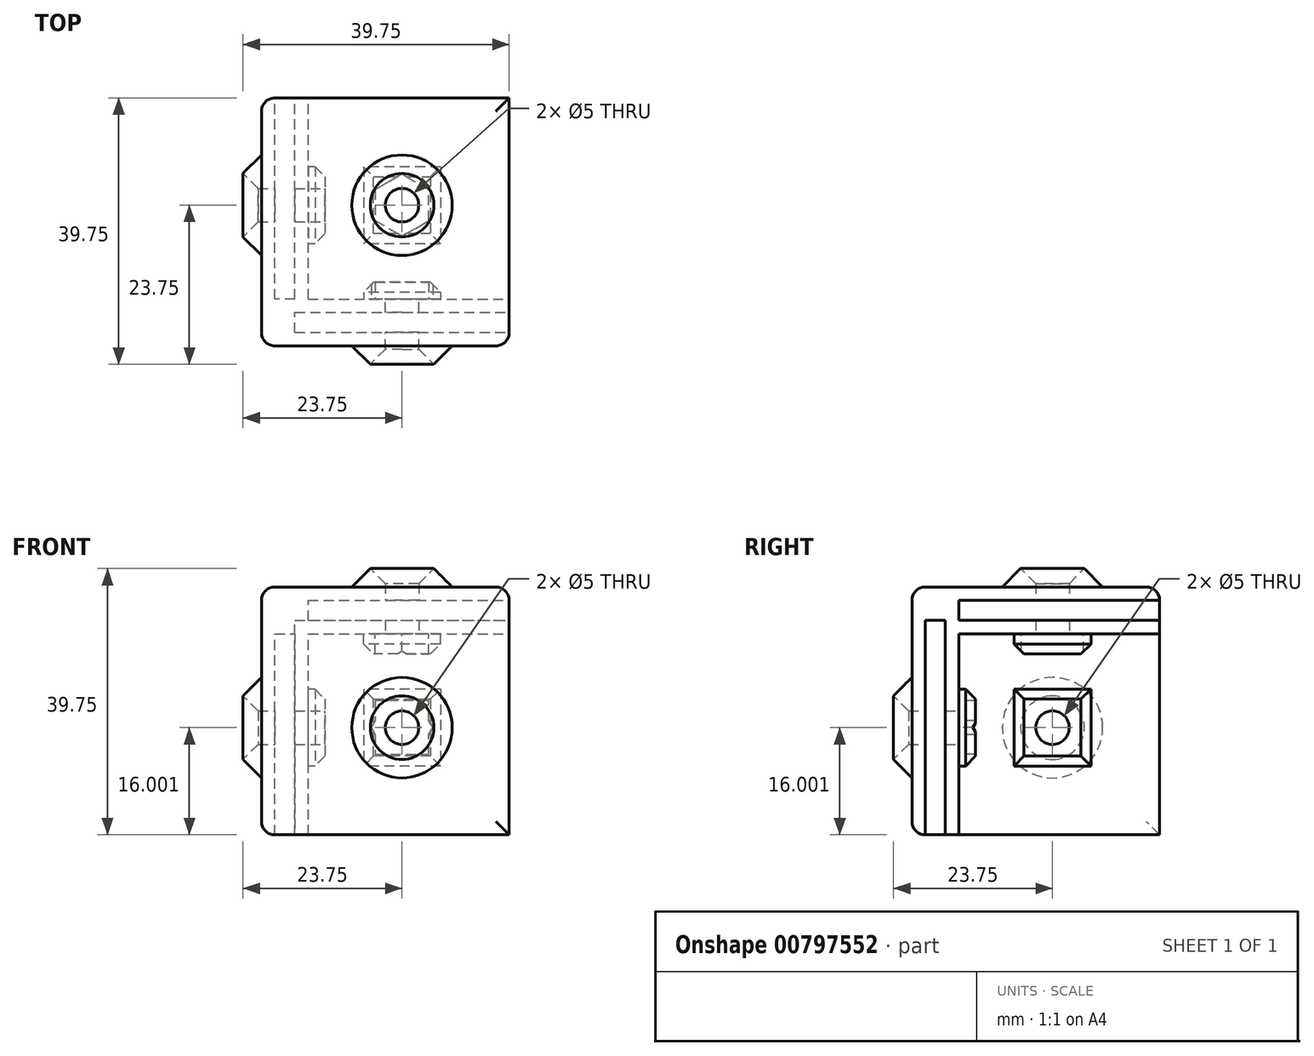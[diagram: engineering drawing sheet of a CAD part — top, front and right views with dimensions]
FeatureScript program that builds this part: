
annotation { "Feature Type Name" : "Feature", "Feature Type Description" : "" }
export const myFeature = defineFeature(function(context is Context, id is Id, definition is map)
    precondition{}
    {
        {
            var Q0;
            Q0=qCreatedBy(makeId("Right.planeOp"),FACE);
            var sketch = newSketch(context, id + "F0", { "sketchPlane" : qUnion([Q0])});
            skLineSegment(sketch, "E0.bottom", {"start": v(0, 0.7) * mm, "end": v(37, 0.7) * mm});
            skLineSegment(sketch, "E0.top", {"start": v(0, 37.7) * mm, "end": v(37, 37.7) * mm});
            skLineSegment(sketch, "E0.left", {"start": v(0, 0.7) * mm, "end": v(0, 37.7) * mm});
            skLineSegment(sketch, "E0.right", {"start": v(37, 0.7) * mm, "end": v(37, 37.7) * mm});
            skSolve(sketch);
        }
        {
            var Q0;
            Q0 = qSketchRegion(id + "F0", true);
            extrude(context, id + "F1", {"entities" : qUnion([Q0]), "depth" : 37 * mm, "offsetDistance" : 25 * mm});
        }
        {
            var Q0;
            Q0=makeQuery(id+"F1.opExtrude","CAP_FACE",FACE,{"disambiguationData":[OSD([sQuery(id+"F0.wireOp",EDGE,"E0.bottom"),sQuery(id+"F0.wireOp",EDGE,"E0.top"),sQuery(id+"F0.wireOp",EDGE,"E0.left"),sQuery(id+"F0.wireOp",EDGE,"E0.right")])],"isStart":false});
            var sketch = newSketch(context, id + "F2", { "sketchPlane" : qUnion([Q0])});
            skLineSegment(sketch, "E1", {"start": v(0, 0.7) * mm, "end": v(2, 0.7) * mm});
            skLineSegment(sketch, "E2", {"start": v(2, 0.7) * mm, "end": v(2, 30.7) * mm});
            skLineSegment(sketch, "E3", {"start": v(2, 30.7) * mm, "end": v(5, 30.7) * mm});
            skLineSegment(sketch, "E4", {"start": v(5, 30.7) * mm, "end": v(5, 0.7) * mm});
            skLineSegment(sketch, "E5", {"start": v(37, 37.7) * mm, "end": v(37, 35.7) * mm});
            skLineSegment(sketch, "E6", {"start": v(37, 35.7) * mm, "end": v(7, 35.7) * mm});
            skLineSegment(sketch, "E7", {"start": v(7, 35.7) * mm, "end": v(7, 32.7) * mm});
            skLineSegment(sketch, "E8", {"start": v(7, 32.7) * mm, "end": v(37, 32.7) * mm});
            skLineSegment(sketch, "E9", {"start": v(5, 0.7) * mm, "end": v(7, 0.7) * mm});
            skLineSegment(sketch, "E10", {"start": v(7, 0.7) * mm, "end": v(7, 30.7) * mm});
            skLineSegment(sketch, "E11", {"start": v(7, 30.7) * mm, "end": v(37, 30.7) * mm});
            skSolve(sketch);
        }
        {
            var Q0;
            Q0 = qSketchRegion(id + "F2", true);
            var Q1;
            {var subQ0=sQuery(id+"F2.wireOp",EDGE,"E10");Q1=makeQuery(id+"F2.imprint","IMPRINT",FACE,{"disambiguationData":[TD([[makeQuery(id+"F2.imprint","IMPRINT",EDGE,{"derivedFrom":subQ0}),-1.0]])]});}
            var Q2;
            {var subQ0=sQuery(id+"F2.wireOp",EDGE,"E2");Q2=makeQuery(id+"F2.imprint","IMPRINT",FACE,{"disambiguationData":[TD([[makeQuery(id+"F2.imprint","IMPRINT",EDGE,{"derivedFrom":subQ0}),-1.0]])]});}
            var Q3;
            {var subQ0=sQuery(id+"F2.wireOp",EDGE,"E6");Q3=makeQuery(id+"F2.imprint","IMPRINT",FACE,{"disambiguationData":[TD([[makeQuery(id+"F2.imprint","IMPRINT",EDGE,{"derivedFrom":subQ0}),1.0]])]});}
            extrude(context, id + "F3", {"entities" : qUnion([Q0, Q1, Q2, Q3]), "operationType" : NewBodyOperationType.REMOVE, "oppositeDirection" : true, "depth" : 30 * mm, "offsetDistance" : 25 * mm});
        }
        {
            var Q0;
            Q0=makeQuery(id+"F1.opExtrude","SWEPT_FACE",FACE,{"disambiguationData":[OSD([sQuery(id+"F0.wireOp",EDGE,"E0.right")])]});
            var sketch = newSketch(context, id + "F4", { "sketchPlane" : qUnion([Q0])});
            skLineSegment(sketch, "E12", {"start": v(0, 0.7) * mm, "end": v(-2, 0.7) * mm});
            skLineSegment(sketch, "E13", {"start": v(-2, 0.7) * mm, "end": v(-2, 30.7) * mm});
            skLineSegment(sketch, "E14", {"start": v(-2, 30.7) * mm, "end": v(-5, 30.7) * mm});
            skLineSegment(sketch, "E15", {"start": v(-5, 30.7) * mm, "end": v(-5, 0.7) * mm});
            skSolve(sketch);
        }
        {
            var Q0;
            Q0 = qSketchRegion(id + "F4", true);
            var Q1;
            {var subQ0=sQuery(id+"F4.wireOp",EDGE,"E13");Q1=makeQuery(id+"F4.imprint","IMPRINT",FACE,{"disambiguationData":[TD([[makeQuery(id+"F4.imprint","IMPRINT",EDGE,{"derivedFrom":subQ0}),1.0]])]});}
            extrude(context, id + "F5", {"entities" : qUnion([Q0, Q1]), "operationType" : NewBodyOperationType.REMOVE, "oppositeDirection" : true, "depth" : 30 * mm, "offsetDistance" : 25 * mm});
        }
        {
            var Q0;
            Q0=makeQuery(id+"F1.opExtrude","CAP_EDGE",EDGE,{"disambiguationData":[OSD([sQuery(id+"F0.wireOp",EDGE,"E0.top")])],"isStart":true});
            var Q1;
            Q1=makeQuery(id+"F1.opExtrude","SWEPT_FACE",FACE,{"disambiguationData":[OSD([sQuery(id+"F0.wireOp",EDGE,"E0.left")])]});
            var Q2;
            Q2=makeQuery(id+"F1.opExtrude","CAP_EDGE",EDGE,{"disambiguationData":[OSD([sQuery(id+"F0.wireOp",EDGE,"E0.top")])],"isStart":false});
            var Q3;
            Q3=makeQuery(id+"F1.opExtrude","SWEPT_EDGE",EDGE,{"disambiguationData":[OSD([sQuery(id+"F0.wireOp",EDGE,"E0.top"),sQuery(id+"F0.wireOp",EDGE,"E0.right")])]});
            var Q4;
            Q4=makeQuery(id+"F1.opExtrude","CAP_EDGE",EDGE,{"disambiguationData":[OSD([sQuery(id+"F0.wireOp",EDGE,"E0.right")])],"isStart":true});
            var Q5;
            Q5=makeQuery(id+"F1.opExtrude","CAP_EDGE",EDGE,{"disambiguationData":[OSD([sQuery(id+"F0.wireOp",EDGE,"E0.bottom")])],"isStart":true});
            var Q6;
            {var subQ0=sQuery(id+"F0.wireOp",EDGE,"E0.bottom");var subQ1=makeQuery(id+"F1.opExtrude","CAP_EDGE",EDGE,{"disambiguationData":[OSD([subQ0])],"isStart":false});Q6=makeQuery(id+"F3.boolean.opBoolean","COPY",EDGE,{"derivedFrom":makeQuery(id+"F3.opExtrude","CAP_EDGE",EDGE,{"disambiguationData":[OSD([subQ0]),TDD([makeQuery(id+"F2.imprint","IMPRINT",EDGE,{"disambiguationData":[TD([[makeQuery(id+"F2.imprint","INTERSECT",VERTEX,{"derivedFrom":[subQ1,makeQuery(id+"F1.opExtrude","CAP_EDGE",EDGE,{"disambiguationData":[OSD([sQuery(id+"F0.wireOp",EDGE,"E0.right")])],"isStart":false})]}),1.0]])],"derivedFrom":subQ1})])],"isStart":false})});}
            var Q7;
            {var subQ0=sQuery(id+"F0.wireOp",EDGE,"E0.right");var subQ1=makeQuery(id+"F1.opExtrude","CAP_EDGE",EDGE,{"disambiguationData":[OSD([subQ0])],"isStart":false});Q7=makeQuery(id+"F3.boolean.opBoolean","COPY",EDGE,{"derivedFrom":makeQuery(id+"F3.opExtrude","CAP_EDGE",EDGE,{"disambiguationData":[OSD([subQ0]),TDD([makeQuery(id+"F2.imprint","IMPRINT",EDGE,{"disambiguationData":[TD([[makeQuery(id+"F2.imprint","INTERSECT",VERTEX,{"derivedFrom":[makeQuery(id+"F1.opExtrude","CAP_EDGE",EDGE,{"disambiguationData":[OSD([sQuery(id+"F0.wireOp",EDGE,"E0.bottom")])],"isStart":false}),subQ1]}),-1.0]])],"derivedFrom":subQ1})])],"isStart":false})});}
            var Q8;
            Q8=makeQuery(id+"F3.boolean.opBoolean","COPY",EDGE,{"derivedFrom":makeQuery(id+"F3.opExtrude","SWEPT_EDGE",EDGE,{"disambiguationData":[OSD([sQuery(id+"F0.wireOp",EDGE,"E0.right"),sQuery(id+"F2.wireOp",EDGE,"E11")])]})});
            var Q9;
            Q9=makeQuery(id+"F3.boolean.opBoolean","COPY",EDGE,{"derivedFrom":makeQuery(id+"F3.opExtrude","CAP_EDGE",EDGE,{"disambiguationData":[OSD([sQuery(id+"F2.wireOp",EDGE,"E11")])],"isStart":true})});
            var Q10;
            Q10=makeQuery(id+"F3.boolean.opBoolean","COPY",EDGE,{"derivedFrom":makeQuery(id+"F3.opExtrude","SWEPT_EDGE",EDGE,{"disambiguationData":[OSD([sQuery(id+"F0.wireOp",EDGE,"E0.bottom"),sQuery(id+"F2.wireOp",EDGE,"E9"),sQuery(id+"F2.wireOp",EDGE,"E10")])]})});
            var Q11;
            Q11=makeQuery(id+"F3.boolean.opBoolean","COPY",EDGE,{"derivedFrom":makeQuery(id+"F3.opExtrude","CAP_EDGE",EDGE,{"disambiguationData":[OSD([sQuery(id+"F2.wireOp",EDGE,"E10")])],"isStart":true})});
            fillet(context, id + "F6", {"entities" : qUnion([Q0, Q1, Q2, Q3, Q4, Q5, Q6, Q7, Q8, Q9, Q10, Q11]), "radius" : 2 * mm, "tangentPropagation" : true, "allowEdgeOverflow" : false});
        }
        {
            var Q0;
            Q0=makeQuery(id+"F3.boolean.opBoolean","COPY",FACE,{"derivedFrom":makeQuery(id+"F3.opExtrude","SWEPT_FACE",FACE,{"disambiguationData":[OSD([sQuery(id+"F2.wireOp",EDGE,"E10")])]})});
            var sketch = newSketch(context, id + "F7", { "sketchPlane" : qUnion([Q0])});
            skCircle(sketch, "E16", {"center": v(-21, 16.7) * mm, "radius": 2.5 * mm});
            skSolve(sketch);
        }
        {
            var Q0;
            Q0=makeQuery(id+"F7.imprint","IMPRINT",FACE,{"disambiguationData":[TD([[makeQuery(id+"F7.imprint","IMPRINT",EDGE,{"derivedFrom":sQuery(id+"F7.wireOp",EDGE,"E16")}),1.0]])]});
            extrude(context, id + "F8", {"entities" : qUnion([Q0]), "operationType" : NewBodyOperationType.REMOVE, "oppositeDirection" : true, "depth" : 25 * mm, "offsetDistance" : 25 * mm});
        }
        {
            var Q0;
            Q0=makeQuery(id+"F1.opExtrude","SWEPT_FACE",FACE,{"disambiguationData":[OSD([sQuery(id+"F0.wireOp",EDGE,"E0.left")])]});
            var sketch = newSketch(context, id + "F9", { "sketchPlane" : qUnion([Q0])});
            skCircle(sketch, "E17", {"center": v(21, 16.7) * mm, "radius": 7.5 * mm});
            skSolve(sketch);
        }
        {
            var Q0;
            Q0=makeQuery(id+"F9.imprint","IMPRINT",FACE,{"disambiguationData":[TD([[makeQuery(id+"F9.imprint","IMPRINT",EDGE,{"derivedFrom":sQuery(id+"F9.wireOp",EDGE,"E17")}),1.0]])]});
            extrude(context, id + "F10", {"entities" : qUnion([Q0]), "operationType" : NewBodyOperationType.ADD, "depth" : 3 * mm, "offsetDistance" : 25 * mm});
        }
        {
            var Q0;
            Q0=makeQuery(id+"F10.opExtrude","CAP_EDGE",EDGE,{"disambiguationData":[OSD([sQuery(id+"F0.wireOp",EDGE,"E0.left"),sQuery(id+"F7.wireOp",EDGE,"E16")])],"isStart":false});
            chamfer(context, id + "F11", {"entities" : qUnion([Q0]), "width" : 2.5 * mm, "tangentPropagation" : true});
        }
        {
            var Q0;
            Q0=makeQuery(id+"F3.boolean.opBoolean","COPY",FACE,{"derivedFrom":makeQuery(id+"F3.opExtrude","SWEPT_FACE",FACE,{"disambiguationData":[OSD([sQuery(id+"F2.wireOp",EDGE,"E10")])]})});
            var sketch = newSketch(context, id + "F12", { "sketchPlane" : qUnion([Q0])});
            skLineSegment(sketch, "E18", {"start": v(-25, 16.7) * mm, "end": v(-25, 20.7) * mm});
            skLineSegment(sketch, "E19", {"start": v(-25, 20.7) * mm, "end": v(-17, 20.7) * mm});
            skLineSegment(sketch, "E20", {"start": v(-17, 20.7) * mm, "end": v(-17, 12.7) * mm});
            skLineSegment(sketch, "E21", {"start": v(-17, 12.7) * mm, "end": v(-25, 12.7) * mm});
            skLineSegment(sketch, "E22", {"start": v(-25, 12.7) * mm, "end": v(-25, 16.7) * mm});
            skLineSegment(sketch, "E23.bottom", {"start": v(-26.75, 22.45) * mm, "end": v(-15.25, 22.45) * mm});
            skLineSegment(sketch, "E23.top", {"start": v(-26.75, 10.95) * mm, "end": v(-15.25, 10.95) * mm});
            skLineSegment(sketch, "E23.left", {"start": v(-26.75, 22.45) * mm, "end": v(-26.75, 10.95) * mm});
            skLineSegment(sketch, "E23.right", {"start": v(-15.25, 22.45) * mm, "end": v(-15.25, 10.95) * mm});
            skPoint(sketch, "E23.middle", {"position": v(-21, 16.7) * mm});
            skLineSegment(sketch, "E24", {"start": v(-25, 20.7) * mm, "end": v(-22.66, 20.7) * mm});
            skLineSegment(sketch, "E25", {"start": v(-25, 20.7) * mm, "end": v(-25, 18.36) * mm});
            skLineSegment(sketch, "E26", {"start": v(-17, 12.7) * mm, "end": v(-19.34, 12.7) * mm});
            skLineSegment(sketch, "E27", {"start": v(-17, 12.7) * mm, "end": v(-17, 15.04) * mm});
            skLineSegment(sketch, "E28", {"start": v(-25, 12.7) * mm, "end": v(-25, 15.04) * mm});
            skLineSegment(sketch, "E29", {"start": v(-17, 20.7) * mm, "end": v(-19.34, 20.7) * mm});
            skLineSegment(sketch, "E30", {"start": v(-17, 18.36) * mm, "end": v(-17, 20.7) * mm});
            skLineSegment(sketch, "E31", {"start": v(-19.34, 12.7) * mm, "end": v(-22.66, 12.7) * mm});
            skCircle(sketch, "E32.cCircle", {"center": v(-21, 16.7) * mm, "radius": 4 * mm, "construction": true});
            skLineSegment(sketch, "E32.0", {"start": v(-23.3, 20.7) * mm, "end": v(-18.7, 20.7) * mm});
            skLineSegment(sketch, "E32.1", {"start": v(-18.7, 20.7) * mm, "end": v(-16.38, 16.7) * mm});
            skLineSegment(sketch, "E32.2", {"start": v(-16.38, 16.7) * mm, "end": v(-18.7, 12.7) * mm});
            skLineSegment(sketch, "E32.3", {"start": v(-18.7, 12.7) * mm, "end": v(-23.3, 12.7) * mm});
            skLineSegment(sketch, "E32.4", {"start": v(-23.3, 12.7) * mm, "end": v(-25.62, 16.7) * mm});
            skLineSegment(sketch, "E32.5", {"start": v(-25.62, 16.7) * mm, "end": v(-23.3, 20.7) * mm});
            skPoint(sketch, "E32.0.midPoint", {"position": v(-21, 20.7) * mm});
            skSolve(sketch);
        }
        {
            var Q0;
            {var subQ0=sQuery(id+"F12.wireOp",EDGE,"E28");Q0=makeQuery(id+"F12.imprint","IMPRINT",FACE,{"disambiguationData":[TD([[makeQuery(id+"F12.imprint","IMPRINT",EDGE,{"derivedFrom":subQ0}),-1.0]])]});}
            var Q1;
            Q1=makeQuery(id+"F12.imprint","IMPRINT",FACE,{"disambiguationData":[TD([[makeQuery(id+"F12.imprint","IMPRINT",EDGE,{"derivedFrom":sQuery(id+"F12.wireOp",EDGE,"E26")}),-1.0]])]});
            var Q2;
            {var subQ18=sQuery(id+"F12.wireOp",EDGE,"E21");Q2=makeQuery(id+"F12.imprint","IMPRINT",FACE,{"disambiguationData":[TD([[makeQuery(id+"F12.imprint","IMPRINT",EDGE,{"derivedFrom":subQ18}),1.0]])]});}
            var Q3;
            {var subQ4=sQuery(id+"F12.wireOp",EDGE,"E24");Q3=makeQuery(id+"F12.imprint","IMPRINT",FACE,{"disambiguationData":[TD([[makeQuery(id+"F12.imprint","IMPRINT",EDGE,{"derivedFrom":subQ4}),-1.0]])]});}
            var Q4;
            {var subQ4=sQuery(id+"F12.wireOp",EDGE,"E29");Q4=makeQuery(id+"F12.imprint","IMPRINT",FACE,{"disambiguationData":[TD([[makeQuery(id+"F12.imprint","IMPRINT",EDGE,{"derivedFrom":subQ4}),1.0]])]});}
            extrude(context, id + "F13", {"entities" : qUnion([Q0, Q1, Q2, Q3, Q4]), "operationType" : NewBodyOperationType.ADD, "depth" : 2.5 * mm, "offsetDistance" : 25 * mm});
        }
        {
            var Q0;
            Q0=makeQuery(id+"F13.opExtrude","CAP_EDGE",EDGE,{"disambiguationData":[OSD([sQuery(id+"F12.wireOp",EDGE,"E23.left")])],"isStart":false});
            var Q1;
            Q1=makeQuery(id+"F13.opExtrude","CAP_EDGE",EDGE,{"disambiguationData":[OSD([sQuery(id+"F12.wireOp",EDGE,"E23.top")])],"isStart":false});
            var Q2;
            Q2=makeQuery(id+"F13.opExtrude","CAP_EDGE",EDGE,{"disambiguationData":[OSD([sQuery(id+"F12.wireOp",EDGE,"E23.right")])],"isStart":false});
            var Q3;
            Q3=makeQuery(id+"F13.opExtrude","CAP_EDGE",EDGE,{"disambiguationData":[OSD([sQuery(id+"F12.wireOp",EDGE,"E23.bottom")])],"isStart":false});
            chamfer(context, id + "F14", {"entities" : qUnion([Q0, Q1, Q2, Q3]), "width" : 1.5 * mm, "tangentPropagation" : true});
        }
        {
            var Q0;
            Q0=makeQuery(id+"F3.boolean.opBoolean","COPY",FACE,{"derivedFrom":makeQuery(id+"F3.opExtrude","CAP_FACE",FACE,{"disambiguationData":[OSD([sQuery(id+"F0.wireOp",EDGE,"E0.bottom"),sQuery(id+"F0.wireOp",EDGE,"E0.right"),sQuery(id+"F2.wireOp",EDGE,"E10"),sQuery(id+"F2.wireOp",EDGE,"E11")])],"isStart":false})});
            var sketch = newSketch(context, id + "F15", { "sketchPlane" : qUnion([Q0])});
            skLineSegment(sketch, "E33", {"start": v(21, 2.7) * mm, "end": v(21, 16.7) * mm});
            skCircle(sketch, "E34", {"center": v(21, 16.7) * mm, "radius": 2.5 * mm});
            skSolve(sketch);
        }
        {
            var Q0;
            Q0=makeQuery(id+"F15.imprint","IMPRINT",FACE,{"disambiguationData":[TD([[makeQuery(id+"F15.imprint","IMPRINT",EDGE,{"derivedFrom":sQuery(id+"F15.wireOp",EDGE,"E34")}),1.0]])]});
            extrude(context, id + "F16", {"entities" : qUnion([Q0]), "operationType" : NewBodyOperationType.REMOVE, "oppositeDirection" : true, "depth" : 25 * mm, "offsetDistance" : 25 * mm});
        }
        {
            var Q0;
            Q0=makeQuery(id+"F1.opExtrude","CAP_FACE",FACE,{"disambiguationData":[OSD([sQuery(id+"F0.wireOp",EDGE,"E0.bottom"),sQuery(id+"F0.wireOp",EDGE,"E0.top"),sQuery(id+"F0.wireOp",EDGE,"E0.left"),sQuery(id+"F0.wireOp",EDGE,"E0.right")])],"isStart":true});
            var sketch = newSketch(context, id + "F17", { "sketchPlane" : qUnion([Q0])});
            skCircle(sketch, "E35", {"center": v(-21, 16.7) * mm, "radius": 7.5 * mm});
            skSolve(sketch);
        }
        {
            var Q0;
            Q0=makeQuery(id+"F17.imprint","IMPRINT",FACE,{"disambiguationData":[TD([[makeQuery(id+"F17.imprint","IMPRINT",EDGE,{"derivedFrom":sQuery(id+"F17.wireOp",EDGE,"E35")}),1.0]])]});
            extrude(context, id + "F18", {"entities" : qUnion([Q0]), "operationType" : NewBodyOperationType.ADD, "depth" : 3 * mm, "offsetDistance" : 25 * mm});
        }
        {
            var Q0;
            Q0=makeQuery(id+"F18.opExtrude","CAP_EDGE",EDGE,{"disambiguationData":[OSD([sQuery(id+"F0.wireOp",EDGE,"E0.bottom"),sQuery(id+"F0.wireOp",EDGE,"E0.top"),sQuery(id+"F0.wireOp",EDGE,"E0.left"),sQuery(id+"F0.wireOp",EDGE,"E0.right"),sQuery(id+"F15.wireOp",EDGE,"E34")])],"isStart":false});
            chamfer(context, id + "F19", {"entities" : qUnion([Q0]), "width" : 2.5 * mm, "tangentPropagation" : true});
        }
        {
            var Q0;
            Q0=makeQuery(id+"F3.boolean.opBoolean","COPY",FACE,{"derivedFrom":makeQuery(id+"F3.opExtrude","CAP_FACE",FACE,{"disambiguationData":[OSD([sQuery(id+"F0.wireOp",EDGE,"E0.bottom"),sQuery(id+"F0.wireOp",EDGE,"E0.right"),sQuery(id+"F2.wireOp",EDGE,"E10"),sQuery(id+"F2.wireOp",EDGE,"E11")])],"isStart":false})});
            var sketch = newSketch(context, id + "F20", { "sketchPlane" : qUnion([Q0])});
            skLineSegment(sketch, "E36.bottom", {"start": v(26.75, 10.95) * mm, "end": v(15.25, 10.95) * mm});
            skLineSegment(sketch, "E36.top", {"start": v(26.75, 22.45) * mm, "end": v(15.25, 22.45) * mm});
            skLineSegment(sketch, "E36.left", {"start": v(26.75, 10.95) * mm, "end": v(26.75, 22.45) * mm});
            skLineSegment(sketch, "E36.right", {"start": v(15.25, 10.95) * mm, "end": v(15.25, 22.45) * mm});
            skPoint(sketch, "E36.middle", {"position": v(21, 16.7) * mm});
            skLineSegment(sketch, "E37.top", {"start": v(25, 20.7) * mm, "end": v(17, 20.7) * mm});
            skLineSegment(sketch, "E38", {"start": v(22.66, 12.7) * mm, "end": v(22.57, 12.62) * mm});
            skLineSegment(sketch, "E39", {"start": v(25, 20.7) * mm, "end": v(22.66, 20.7) * mm});
            skLineSegment(sketch, "E40", {"start": v(25, 20.7) * mm, "end": v(25, 18.36) * mm});
            skCircle(sketch, "E41.cCircle", {"center": v(21, 16.7) * mm, "radius": 4 * mm, "construction": true});
            skLineSegment(sketch, "E41.0", {"start": v(18.7, 20.7) * mm, "end": v(23.3, 20.7) * mm});
            skLineSegment(sketch, "E41.1", {"start": v(23.3, 20.7) * mm, "end": v(25.62, 16.7) * mm});
            skLineSegment(sketch, "E41.2", {"start": v(25.62, 16.7) * mm, "end": v(23.3, 12.7) * mm});
            skLineSegment(sketch, "E41.3", {"start": v(23.3, 12.7) * mm, "end": v(18.7, 12.7) * mm});
            skLineSegment(sketch, "E41.4", {"start": v(18.7, 12.7) * mm, "end": v(16.38, 16.7) * mm});
            skLineSegment(sketch, "E41.5", {"start": v(16.38, 16.7) * mm, "end": v(18.7, 20.7) * mm});
            skPoint(sketch, "E41.0.midPoint", {"position": v(21, 20.7) * mm});
            skSolve(sketch);
        }
        {
            var Q0;
            Q0=makeQuery(id+"F20.imprint","IMPRINT",FACE,{"disambiguationData":[TD([[makeQuery(id+"F20.imprint","IMPRINT",EDGE,{"derivedFrom":sQuery(id+"F20.wireOp",EDGE,"E36.bottom")}),-1.0]])]});
            var Q1;
            {var subQ0=sQuery(id+"F20.wireOp",EDGE,"eGdclESt-ae4Q-qKfY-z9fV-YHrHrvBsCehK");Q1=makeQuery(id+"F20.imprint","IMPRINT",FACE,{"disambiguationData":[TD([[makeQuery(id+"F20.imprint","IMPRINT",EDGE,{"derivedFrom":subQ0}),-1.0]])]});}
            var Q2;
            {var subQ0=sQuery(id+"F20.wireOp",EDGE,"eGdclESt-ae4Q-qKfY-z9fV-YHrHrvBsCehK");Q2=makeQuery(id+"F20.imprint","IMPRINT",FACE,{"disambiguationData":[TD([[makeQuery(id+"F20.imprint","IMPRINT",EDGE,{"derivedFrom":subQ0}),1.0]])]});}
            var Q3;
            Q3=makeQuery(id+"F20.imprint","IMPRINT",FACE,{"disambiguationData":[TD([[makeQuery(id+"F20.imprint","IMPRINT",EDGE,{"derivedFrom":sQuery(id+"F20.wireOp",EDGE,"5zauiICW-kTdx-xMl5-GpjY-PmGtw9wtqw4C")}),-1.0]])]});
            var Q4;
            Q4=makeQuery(id+"F20.imprint","IMPRINT",FACE,{"disambiguationData":[TD([[makeQuery(id+"F20.imprint","IMPRINT",EDGE,{"derivedFrom":sQuery(id+"F20.wireOp",EDGE,"E39")}),1.0]])]});
            var Q5;
            {var subQ0=sQuery(id+"F20.wireOp",EDGE,"E37.right");var subQ1=sQuery(id+"F20.wireOp",EDGE,"E37.top");var subQ2=makeQuery(id+"F20.imprint","INTERSECT",VERTEX,{"derivedFrom":[subQ1,subQ0]});Q5=makeQuery(id+"F20.imprint","IMPRINT",FACE,{"disambiguationData":[TD([[makeQuery(id+"F20.imprint","IMPRINT",EDGE,{"disambiguationData":[TD([[subQ2,1.0]])],"derivedFrom":subQ1}),1.0]])]});}
            extrude(context, id + "F21", {"entities" : qUnion([Q0, Q1, Q2, Q3, Q4, Q5]), "operationType" : NewBodyOperationType.ADD, "depth" : 2.5 * mm, "offsetDistance" : 25 * mm});
        }
        {
            var Q0;
            Q0=makeQuery(id+"F21.opExtrude","CAP_EDGE",EDGE,{"disambiguationData":[OSD([sQuery(id+"F20.wireOp",EDGE,"E36.left")])],"isStart":false});
            var Q1;
            Q1=makeQuery(id+"F21.opExtrude","CAP_EDGE",EDGE,{"disambiguationData":[OSD([sQuery(id+"F20.wireOp",EDGE,"E36.top")])],"isStart":false});
            var Q2;
            Q2=makeQuery(id+"F21.opExtrude","CAP_EDGE",EDGE,{"disambiguationData":[OSD([sQuery(id+"F20.wireOp",EDGE,"E36.right")])],"isStart":false});
            var Q3;
            Q3=makeQuery(id+"F21.opExtrude","CAP_EDGE",EDGE,{"disambiguationData":[OSD([sQuery(id+"F20.wireOp",EDGE,"E36.bottom")])],"isStart":false});
            chamfer(context, id + "F22", {"entities" : qUnion([Q0, Q1, Q2, Q3]), "width" : 1.5 * mm, "tangentPropagation" : true});
        }
        {
            var Q0;
            Q0=makeQuery(id+"F3.boolean.opBoolean","COPY",FACE,{"derivedFrom":makeQuery(id+"F3.opExtrude","SWEPT_FACE",FACE,{"disambiguationData":[OSD([sQuery(id+"F2.wireOp",EDGE,"E11")])]})});
            var sketch = newSketch(context, id + "F23", { "sketchPlane" : qUnion([Q0])});
            skCircle(sketch, "E42", {"center": v(21, -21) * mm, "radius": 2.5 * mm});
            skLineSegment(sketch, "E43.bottom", {"start": v(26.75, -26.75) * mm, "end": v(15.25, -26.75) * mm});
            skLineSegment(sketch, "E43.top", {"start": v(26.75, -15.25) * mm, "end": v(15.25, -15.25) * mm});
            skLineSegment(sketch, "E43.left", {"start": v(26.75, -26.75) * mm, "end": v(26.75, -15.25) * mm});
            skLineSegment(sketch, "E43.right", {"start": v(15.25, -26.75) * mm, "end": v(15.25, -15.25) * mm});
            skCircle(sketch, "E44.cCircle", {"center": v(21, -21) * mm, "radius": 4 * mm, "construction": true});
            skLineSegment(sketch, "E44.0", {"start": v(17, -23.3) * mm, "end": v(17, -18.7) * mm});
            skLineSegment(sketch, "E44.1", {"start": v(17, -18.7) * mm, "end": v(21, -16.38) * mm});
            skLineSegment(sketch, "E44.2", {"start": v(21, -16.38) * mm, "end": v(25, -18.7) * mm});
            skLineSegment(sketch, "E44.3", {"start": v(25, -18.7) * mm, "end": v(25, -23.3) * mm});
            skLineSegment(sketch, "E44.4", {"start": v(25, -23.3) * mm, "end": v(21, -25.62) * mm});
            skLineSegment(sketch, "E44.5", {"start": v(21, -25.62) * mm, "end": v(17, -23.3) * mm});
            skPoint(sketch, "E44.0.midPoint", {"position": v(17, -21) * mm});
            skSolve(sketch);
        }
        {
            var Q0;
            Q0=makeQuery(id+"F23.imprint","IMPRINT",FACE,{"disambiguationData":[TD([[makeQuery(id+"F23.imprint","IMPRINT",EDGE,{"derivedFrom":sQuery(id+"F23.wireOp",EDGE,"E42")}),1.0]])]});
            extrude(context, id + "F24", {"entities" : qUnion([Q0]), "operationType" : NewBodyOperationType.REMOVE, "oppositeDirection" : true, "depth" : 25 * mm, "offsetDistance" : 25 * mm});
        }
        {
            var Q0;
            Q0=makeQuery(id+"F1.opExtrude","SWEPT_FACE",FACE,{"disambiguationData":[OSD([sQuery(id+"F0.wireOp",EDGE,"E0.top")])]});
            var sketch = newSketch(context, id + "F25", { "sketchPlane" : qUnion([Q0])});
            skCircle(sketch, "E45", {"center": v(21, 21) * mm, "radius": 7.5 * mm});
            skSolve(sketch);
        }
        {
            var Q0;
            Q0=makeQuery(id+"F25.imprint","IMPRINT",FACE,{"disambiguationData":[TD([[makeQuery(id+"F25.imprint","IMPRINT",EDGE,{"derivedFrom":sQuery(id+"F25.wireOp",EDGE,"E45")}),1.0]])]});
            extrude(context, id + "F26", {"entities" : qUnion([Q0]), "operationType" : NewBodyOperationType.ADD, "depth" : 3 * mm, "offsetDistance" : 25 * mm});
        }
        {
            var Q0;
            Q0=makeQuery(id+"F26.opExtrude","CAP_EDGE",EDGE,{"disambiguationData":[OSD([sQuery(id+"F0.wireOp",EDGE,"E0.top"),sQuery(id+"F23.wireOp",EDGE,"E42")])],"isStart":false});
            chamfer(context, id + "F27", {"entities" : qUnion([Q0]), "width" : 2.5 * mm, "tangentPropagation" : true});
        }
        {
            var Q0;
            Q0=makeQuery(id+"F3.boolean.opBoolean","COPY",FACE,{"derivedFrom":makeQuery(id+"F3.opExtrude","CAP_FACE",FACE,{"disambiguationData":[OSD([sQuery(id+"F0.wireOp",EDGE,"E0.bottom"),sQuery(id+"F2.wireOp",EDGE,"E2"),sQuery(id+"F2.wireOp",EDGE,"E3"),sQuery(id+"F2.wireOp",EDGE,"E4")])],"isStart":false})});
            extrude(context, id + "F28", {"entities" : qUnion([Q0]), "operationType" : NewBodyOperationType.REMOVE, "oppositeDirection" : true, "depth" : 2 * mm, "offsetDistance" : 25 * mm});
        }
        {
            var Q0;
            {var subQ0=sQuery(id+"F2.wireOp",EDGE,"E3");Q0=makeQuery(id+"F28.boolean.opBoolean","MERGE",FACE,{"derivedFrom":[makeQuery(id+"F3.boolean.opBoolean","COPY",FACE,{"derivedFrom":makeQuery(id+"F3.opExtrude","SWEPT_FACE",FACE,{"disambiguationData":[OSD([subQ0])]})}),makeQuery(id+"F28.opExtrude","SWEPT_FACE",FACE,{"disambiguationData":[OSD([subQ0])]})]});}
            extrude(context, id + "F29", {"entities" : qUnion([Q0]), "operationType" : NewBodyOperationType.REMOVE, "oppositeDirection" : true, "depth" : 2 * mm, "offsetDistance" : 25 * mm});
        }
        {
            var Q0;
            Q0=makeQuery(id+"F23.imprint","IMPRINT",FACE,{"disambiguationData":[TD([[makeQuery(id+"F23.imprint","IMPRINT",EDGE,{"derivedFrom":sQuery(id+"F23.wireOp",EDGE,"E43.bottom")}),-1.0]])]});
            extrude(context, id + "F30", {"entities" : qUnion([Q0]), "operationType" : NewBodyOperationType.ADD, "depth" : 3 * mm, "offsetDistance" : 25 * mm});
        }
        {
            var Q0;
            Q0=makeQuery(id+"F30.opExtrude","CAP_EDGE",EDGE,{"disambiguationData":[OSD([sQuery(id+"F23.wireOp",EDGE,"E43.right")])],"isStart":false});
            var Q1;
            Q1=makeQuery(id+"F30.opExtrude","CAP_EDGE",EDGE,{"disambiguationData":[OSD([sQuery(id+"F23.wireOp",EDGE,"E43.bottom")])],"isStart":false});
            var Q2;
            Q2=makeQuery(id+"F30.opExtrude","CAP_EDGE",EDGE,{"disambiguationData":[OSD([sQuery(id+"F23.wireOp",EDGE,"E43.left")])],"isStart":false});
            var Q3;
            Q3=makeQuery(id+"F30.opExtrude","CAP_EDGE",EDGE,{"disambiguationData":[OSD([sQuery(id+"F23.wireOp",EDGE,"E43.top")])],"isStart":false});
            chamfer(context, id + "F31", {"entities" : qUnion([Q0, Q1, Q2, Q3]), "width" : 1.5 * mm, "tangentPropagation" : true});
        }
        {
            var Q0;
            Q0=makeQuery(id+"F10.opExtrude","CAP_EDGE",EDGE,{"disambiguationData":[OSD([sQuery(id+"F9.wireOp",EDGE,"E17")])],"isStart":false});
            var Q1;
            Q1=makeQuery(id+"F18.opExtrude","CAP_EDGE",EDGE,{"disambiguationData":[OSD([sQuery(id+"F17.wireOp",EDGE,"E35")])],"isStart":false});
            var Q2;
            Q2=makeQuery(id+"F26.opExtrude","CAP_EDGE",EDGE,{"disambiguationData":[OSD([sQuery(id+"F25.wireOp",EDGE,"E45")])],"isStart":false});
            chamfer(context, id + "F32", {"entities" : qUnion([Q0, Q1, Q2]), "width" : 3 * mm, "tangentPropagation" : true});
        }
    });
